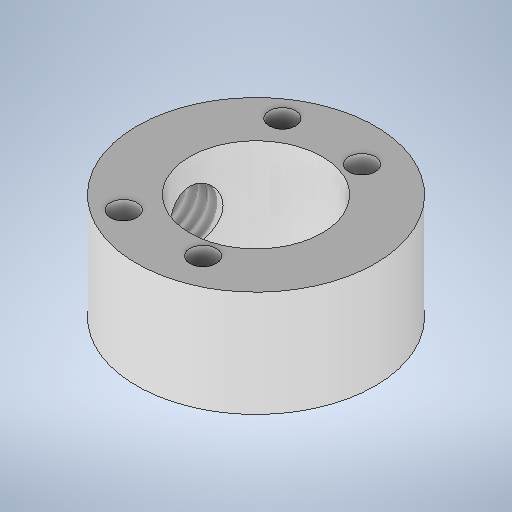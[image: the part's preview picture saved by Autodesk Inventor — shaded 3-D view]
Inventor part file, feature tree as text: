
AUTODESK INVENTOR PART (.ipt)
format: ipt  version: 2025.1 (Build 291241000, 241)  size: 257,536 bytes
history: native  units: mm
features: sketch x3, extrude x2, plane x1, hole x1, projected_geometry x1
ambient origin geometry x8: Origin, YZ Plane, XZ Plane, XY Plane, X Axis, Y Axis, Z Axis, Center Point
bodies: Solid1 (feature_tree)
feature tree (8):
  extrude  "Extrusion1"  Depth=2.0mm
  extrude  "Extrusion2"  Depth=6.0mm
  plane  "Work Plane1"
  hole  "Hole1"  [1 undecoded]
  sketch  "Sketch1"  dims[d0=18.0mm d2=2.0mm]
  sketch  "Sketch2"  dims[d3=12.0mm d4=6.0mm]
  sketch  "Sketch3"  dims[d5=12.0mm d6=4.0mm d7=6.0mm d8=2.0mm d9=8.0mm d10=0.0mm d11=10.0mm d13=18.0mm d14=0.0mm d15=2.0mm d16=-9.0mm d17=4.134mm d18=4.0mm d19=4.0mm d20=2.0mm d21=90.0deg d22=4.5mm d23=0.0mm]
  projected_geometry  "Projected Loop1"
note: 1 required parameter value undecoded (feature->parameter linkage not recoverable at this tier; creation-order binding heuristic only, values carry confidence <= 0.55)
